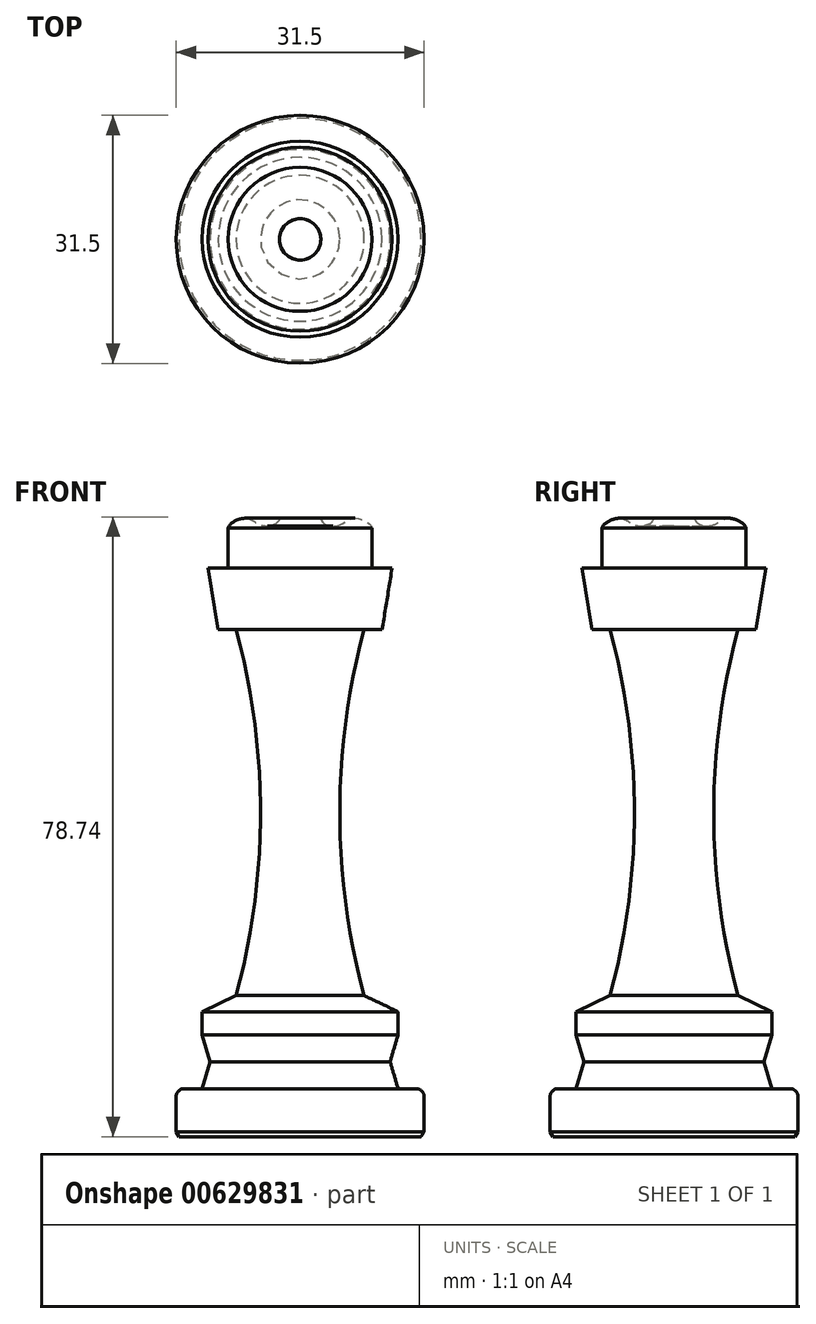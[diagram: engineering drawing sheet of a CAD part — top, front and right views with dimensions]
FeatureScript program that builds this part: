
annotation { "Feature Type Name" : "Feature", "Feature Type Description" : "" }
export const myFeature = defineFeature(function(context is Context, id is Id, definition is map)
    precondition{}
    {
        {
            var Q0;
            Q0=qCreatedBy(makeId("Front.planeOp"),FACE);
            var sketch = newSketch(context, id + "F0", { "sketchPlane" : qUnion([Q0])});
            skLineSegment(sketch, "E0.MirrorCS", {"start": v(15.37, 0) * mm, "end": v(15.75, 0.64) * mm});
            skLineSegment(sketch, "E1.MirrorCS", {"start": v(15.37, 0) * mm, "end": v(0, 0) * mm});
            skLineSegment(sketch, "E2", {"start": v(15.75, 0.64) * mm, "end": v(15.75, 5.08) * mm});
            skArc(sketch, "E3", {"start": v(15.75, 5.08) * mm, "mid": v(15.45, 5.8) * mm, "end": v(14.73, 6.1) * mm});
            skLineSegment(sketch, "E4", {"start": v(14.73, 6.1) * mm, "end": v(12.45, 6.1) * mm});
            skLineSegment(sketch, "E5", {"start": v(12.45, 6.1) * mm, "end": v(11.43, 9.52) * mm});
            skLineSegment(sketch, "E6", {"start": v(11.43, 9.53) * mm, "end": v(12.45, 12.95) * mm});
            skLineSegment(sketch, "E7", {"start": v(12.45, 12.95) * mm, "end": v(12.45, 15.88) * mm});
            skFitSpline(sketch, "E8", {"points": [v(2.63, 78.74) * mm, v(4.79, 77.65) * mm, v(6.86, 78.56) * mm, v(9.18, 77.06) * mm], "startDerivative": vector(-0.1, -9.85) * mm, "endDerivative": vector(0, -7.55) * mm});
            skLineSegment(sketch, "E9", {"start": v(9.14, 77.32) * mm, "end": v(9.14, 72.24) * mm});
            skLineSegment(sketch, "E10", {"start": v(0, 78.74) * mm, "end": v(0, 0) * mm});
            skLineSegment(sketch, "E11", {"start": v(12.45, 15.88) * mm, "end": v(8.13, 17.93) * mm});
            skArc(sketch, "E12", {"start": v(8.13, 64.4) * mm, "mid": v(5.04, 41.17) * mm, "end": v(8.13, 17.93) * mm});
            skArc(sketch, "E13", {"start": v(2.63, 78.74) * mm, "mid": v(1.31, 80.05) * mm, "end": v(0, 78.74) * mm});
            skLineSegment(sketch, "E14", {"start": v(9.14, 72.24) * mm, "end": v(11.68, 72.24) * mm});
            skLineSegment(sketch, "E15", {"start": v(11.68, 72.24) * mm, "end": v(10.41, 64.4) * mm});
            skLineSegment(sketch, "E16", {"start": v(10.41, 64.4) * mm, "end": v(8.13, 64.4) * mm});
            skSolve(sketch);
        }
        {
            var Q0;
            Q0=makeQuery(id+"F0.imprint","IMPRINT",FACE,{"disambiguationData":[TD([[makeQuery(id+"F0.imprint","IMPRINT",EDGE,{"derivedFrom":sQuery(id+"F0.wireOp",EDGE,"E0.MirrorCS")}),1.0]])]});
            var Q1;
            Q1=sQuery(id+"F0.wireOp",EDGE,"E10");
            revolve(context, id + "F1", {"entities" : qUnion([Q0]), "axis" : qUnion([Q1]), "revolveType" : RevolveType.FULL});
        }
    });
